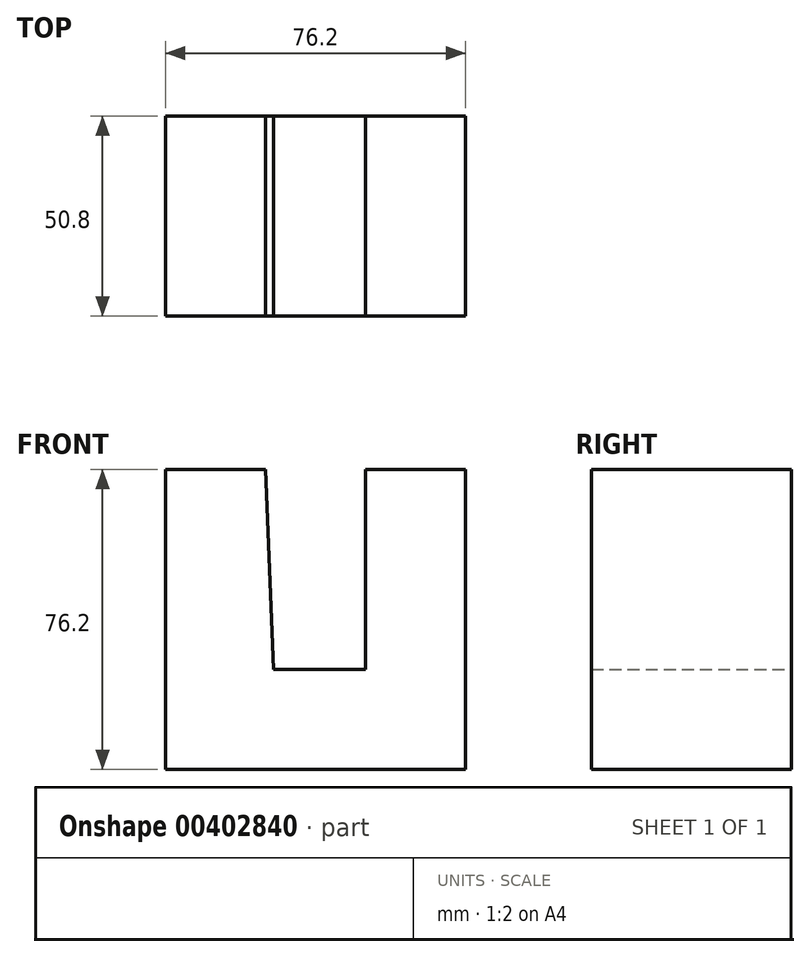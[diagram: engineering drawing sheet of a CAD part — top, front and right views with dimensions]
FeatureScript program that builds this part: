
annotation { "Feature Type Name" : "Feature", "Feature Type Description" : "" }
export const myFeature = defineFeature(function(context is Context, id is Id, definition is map)
    precondition{}
    {
        {
            var Q0;
            Q0=qCreatedBy(makeId("Front.planeOp"),FACE);
            var sketch = newSketch(context, id + "F0", { "sketchPlane" : qUnion([Q0])});
            skLineSegment(sketch, "E0", {"start": v(0, 0) * mm, "end": v(0, 76.2) * mm});
            skLineSegment(sketch, "E1", {"start": v(0, 0) * mm, "end": v(76.2, 0) * mm});
            skLineSegment(sketch, "E2", {"start": v(76.2, 0) * mm, "end": v(76.2, 76.2) * mm});
            skLineSegment(sketch, "E3", {"start": v(76.2, 76.2) * mm, "end": v(50.8, 76.2) * mm});
            skLineSegment(sketch, "E4", {"start": v(50.8, 76.2) * mm, "end": v(50.8, 25.4) * mm});
            skLineSegment(sketch, "E5", {"start": v(0, 76.2) * mm, "end": v(25.4, 76.2) * mm});
            skLineSegment(sketch, "E6", {"start": v(25.4, 76.2) * mm, "end": v(27.41, 25.44) * mm});
            skLineSegment(sketch, "E7", {"start": v(27.41, 25.44) * mm, "end": v(50.8, 25.4) * mm});
            skSolve(sketch);
        }
        {
            var Q0;
            Q0=makeQuery(id+"F0.imprint","IMPRINT",FACE,{"disambiguationData":[TD([[makeQuery(id+"F0.imprint","IMPRINT",EDGE,{"derivedFrom":sQuery(id+"F0.wireOp",EDGE,"E0")}),-1.0]])]});
            extrude(context, id + "F1", {"entities" : qUnion([Q0]), "depth" : 50.8 * mm});
        }
    });
